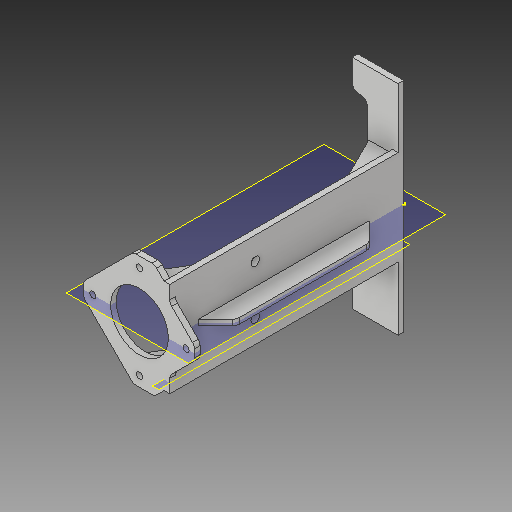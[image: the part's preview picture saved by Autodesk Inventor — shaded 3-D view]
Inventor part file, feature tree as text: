
AUTODESK INVENTOR PART (.ipt)
format: ipt  version: 2018 (Build 220112000, 112)  size: 288,256 bytes
history: native  units: mm
features: reference x14, sketch x12, extrude x10, fillet x3, plane x2, mirror x2, chamfer x1
ambient origin geometry x8: Origin, YZ Plane, XZ Plane, XY Plane, X Axis, Y Axis, Z Axis, Center Point
bodies: Solid1 (feature_tree)
feature tree (44):
  extrude  "Extrusion1"  Depth=13.0mm
  fillet  "Fillet1"  Radius=30.0mm
  extrude  "Extrusion2"  Depth=55.0mm
  extrude  "Extrusion3"  Depth=16.0mm
  extrude  "Extrusion4"  Depth=7.0mm
  extrude  "Extrusion5"  Depth=6.0mm
  chamfer  "Chamfer1"  Distance=241.0mm
  fillet  "Fillet2"  Radius=6.0mm
  extrude  "Extrusion6"  Depth=10.0mm
  extrude  "Extrusion7"  Depth=4.0mm
  plane  "Work Plane1"
  plane  "Work Plane2"
  sketch  "Sketch8"  dims[d20=4.0mm d23=7.0mm d24=0.0mm]
  extrude  "Extrusion8"  Depth=7.0mm TaperAngle=0.0deg
  mirror  "Mirror1"
  extrude  "Extrusion9"  Depth=6.0mm
  mirror  "Mirror2"
  sketch  "Sketch11"  dims[d33=0.5mm]
  extrude  "Extrusion10"  Depth=13.0mm TaperAngle=45.0deg
  fillet  "Fillet3"  Radius=7.0mm
  sketch  "Sketch1"  dims[d0=230.0mm d1=13.0mm d2=30.0mm]
  reference  "Reference1"
  sketch  "Sketch2"  dims[d3=55.0mm d4=55.0mm]
  reference  "Reference2"
  reference  "Reference3"
  sketch  "Sketch3"  dims[d5=55.0mm d6=16.0mm]
  sketch  "Sketch4"  dims[d7=6.0mm d8=0.0mm d9=7.0mm]
  reference  "Reference4"
  reference  "Reference5"
  reference  "Reference6"
  reference  "Reference7"
  sketch  "Sketch5"  dims[d10=100.0mm d11=6.0mm d12=241.0mm d13=0.0mm d14=6.0mm]
  sketch  "Sketch6"  dims[d15=85.0mm d16=0.0mm d17=10.0mm]
  reference  "Reference8"
  reference  "Reference9"
  reference  "Reference10"
  reference  "Reference11"
  reference  "Reference12"
  sketch  "Sketch7"  dims[d18=10.0mm d19=4.0mm]
  reference  "Reference13"
  reference  "Reference14"
  sketch  "Sketch9"  dims[d25=6.0mm d26=40.0mm]
  sketch  "Sketch10"  dims[d27=26.0mm d28=0.0mm d29=13.0mm d30=2.0mm d31=45.0deg d32=7.0mm]
  sketch  "Sketch12"  dims[d34=7.0mm d35=0.0mm d36=7.0mm d37=0.0mm d38=-10.0mm d39=25.0mm d40=50.0mm d41=6.0mm d42=0.0mm d43=30.0mm d45=50.0mm d46=6.0mm d47=0.0mm d48=90.0mm d49=90.0mm d50=90.0deg d51=45.0deg d52=20.0mm d53=6.0mm d54=0.0mm d55=7.0mm]
